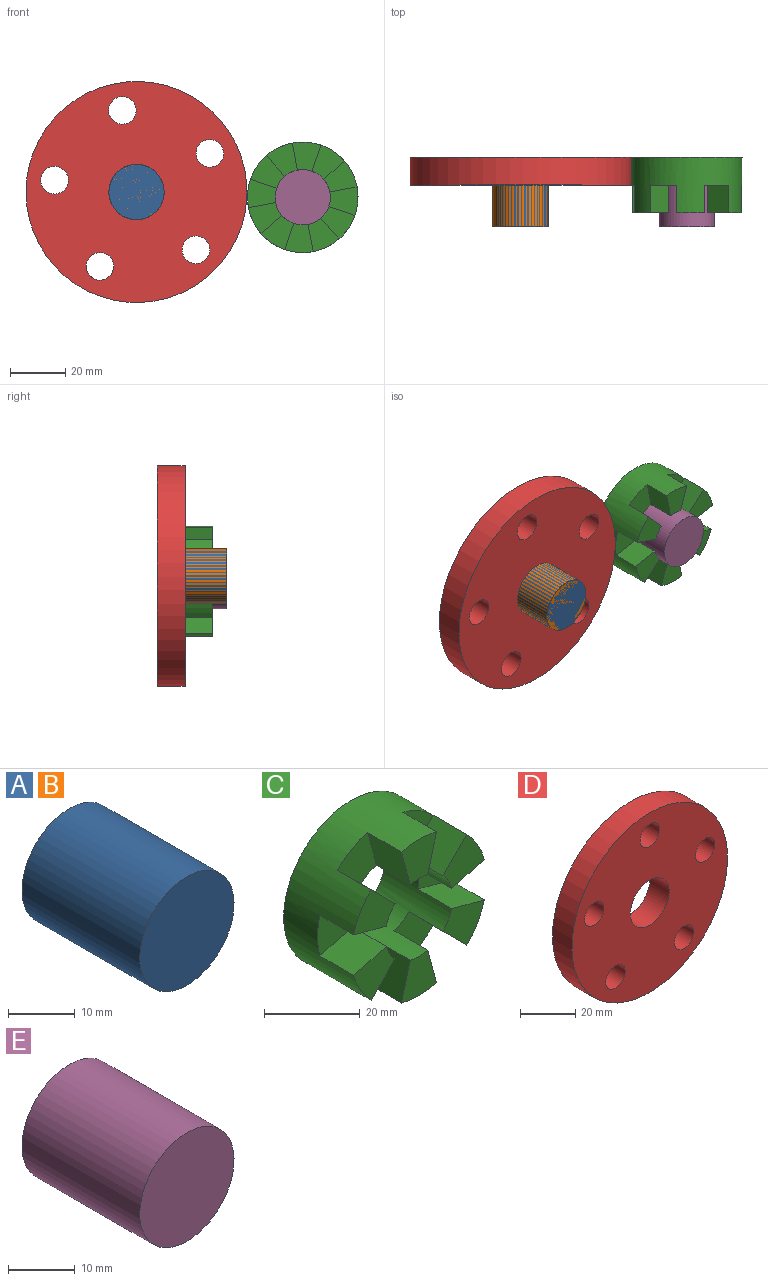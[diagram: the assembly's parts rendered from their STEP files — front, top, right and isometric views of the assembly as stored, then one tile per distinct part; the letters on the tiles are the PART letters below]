
ASSEMBLY  parts=5 mates=4
PART A: 3 faces, bbox 20x25x20 mm
  f0: cylinder r=10mm len=25mm, axis (0,1,0), area 1570.8mm2, adj f1,f2
  f1: plane 20x20mm, normal (0,-1,0), area 314.2mm2, adj f0
  f2: plane 20x20mm, normal (0,1,0), area 314.2mm2, adj f0
PART B: same geometry as A
PART C: 27 faces, bbox 40x20x40 mm
  f0: cylinder r=10mm len=20mm, axis (0,1,0), area 942.5mm2, adj f1,f2,f3,f4,f5,f7,f8,f9
  f1: plane 10.35x10.34mm, normal (0,-1,0), area 78.5mm2, adj f0,f6,f9,f24
  f2: plane 12.25x11.55mm, normal (0,-1,0), area 78.5mm2, adj f0,f6,f21,f25
  f3: plane 12.25x11.55mm, normal (0,-1,0), area 78.5mm2, adj f0,f6,f18,f22
  f4: plane 10.35x10.34mm, normal (0,-1,0), area 78.5mm2, adj f0,f6,f15,f19
  f5: plane 12.25x11.55mm, normal (0,-1,0), area 78.5mm2, adj f0,f6,f12,f16
  f6: cylinder r=20mm len=40mm, axis (0,1,0), area 1885mm2, adj f1,f2,f3,f4,f5,f7,f8,f9
  f7: plane 12.25x11.55mm, normal (0,-1,0), area 78.5mm2, adj f0,f6,f10,f13
  f8: plane 40x40mm, normal (0,1,0), area 942.5mm2, adj f0,f6
  f9: plane 10x9.66mm, normal (-0.97,0,-0.26), area 100mm2, adj f0,f1,f6,f11
  f10: plane 10x7.07mm, normal (0.71,0,0.71), area 100mm2, adj f0,f6,f7,f11
  f11: plane 12.25x11.55mm, normal (0,-1,0), area 78.5mm2, adj f0,f6,f9,f10
  f12: plane 10x9.66mm, normal (-0.26,0,0.97), area 100mm2, adj f0,f5,f6,f14
  f13: plane 10x9.66mm, normal (-0.26,0,-0.97), area 100mm2, adj f0,f6,f7,f14
  f14: plane 10.35x10.34mm, normal (0,-1,0), area 78.5mm2, adj f0,f6,f12,f13
  f15: plane 10x9.66mm, normal (-0.97,0,0.26), area 100mm2, adj f0,f4,f6,f17
  f16: plane 10x7.07mm, normal (0.71,0,-0.71), area 100mm2, adj f0,f5,f6,f17
  f17: plane 12.25x11.55mm, normal (0,-1,0), area 78.5mm2, adj f0,f6,f15,f16
  f18: plane 10x7.07mm, normal (-0.71,0,-0.71), area 100mm2, adj f0,f3,f6,f20
  f19: plane 10x9.66mm, normal (0.97,0,0.26), area 100mm2, adj f0,f4,f6,f20
  f20: plane 12.25x11.55mm, normal (0,-1,0), area 78.5mm2, adj f0,f6,f18,f19
  f21: plane 10x9.66mm, normal (0.26,0,-0.97), area 100mm2, adj f0,f2,f6,f23
  f22: plane 10x9.66mm, normal (0.26,0,0.97), area 100mm2, adj f0,f3,f6,f23
  f23: plane 10.35x10.34mm, normal (0,-1,0), area 78.5mm2, adj f0,f6,f21,f22
  f24: plane 10x9.66mm, normal (0.97,0,-0.26), area 100mm2, adj f0,f1,f6,f26
  f25: plane 10x7.07mm, normal (-0.71,0,0.71), area 100mm2, adj f0,f2,f6,f26
  f26: plane 12.25x11.55mm, normal (0,-1,0), area 78.5mm2, adj f0,f6,f24,f25
PART D: 9 faces, bbox 80x10x80 mm
  f0: plane 80x80mm, normal (0,-1,0), area 4319.7mm2, adj f2,f3,f4,f5,f6,f7,f8
  f1: plane 80x80mm, normal (0,1,0), area 4319.7mm2, adj f2,f3,f4,f5,f6,f7,f8
  f2: cylinder r=40mm len=80mm, axis (0,1,0), area 2513.3mm2, adj f0,f1
  f3: cylinder r=5mm len=10mm, axis (0,-1,0), area 314.2mm2, adj f0,f1
  f4: cylinder r=10mm len=20mm, axis (0,-1,0), area 628.3mm2, adj f0,f1
  f5: cylinder r=5mm len=10mm, axis (0,-1,0), area 314.2mm2, adj f0,f1
  f6: cylinder r=5mm len=10mm, axis (0,-1,0), area 314.2mm2, adj f0,f1
  f7: cylinder r=5mm len=10mm, axis (0,-1,0), area 314.2mm2, adj f0,f1
  f8: cylinder r=5mm len=10mm, axis (0,-1,0), area 314.2mm2, adj f0,f1
PART E: 3 faces, bbox 20x25x20 mm
  f0: cylinder r=10mm len=25mm, axis (0,1,0), area 1570.8mm2, adj f1,f2
  f1: plane 20x20mm, normal (0,-1,0), area 314.2mm2, adj f0
  f2: plane 20x20mm, normal (0,1,0), area 314.2mm2, adj f0
PLACE A at identity fixed
PLACE B rot(axis=(0,1,0),15deg) t=(0,0,0)mm
PLACE C rot(axis=(0,-1,0),55.9deg) t=(64.66,2.5,-37.3)mm
PLACE D rot(axis=(0,-1,0),153.8deg) t=(0,2.5,0)mm
PLACE E rot(axis=(0,-1,0),3.5deg) t=(21.91,12.5,19.02)mm fixed
MATE revolute D.f2 <-> A.f0  axis (0,1,0) through (0,12.5,0)mm
MATE planar C.f0 <-> D.f2  axis (0,1,0) through (60.16,12.5,-1.91)mm
MATE revolute C.f0 <-> E.f0  axis (0,1,0) through (60.16,12.5,-1.91)mm
MATE planar E.f0 <-> D.f2  axis (0,1,0) through (60.16,12.5,-1.91)mm
